# Revit family: LTV8FF
name_source: partatom
category: Lighting Fixtures
units: mm (PartAtom-declared; Revit-internal decimal feet)

## family parameters
Cut with Voids When Loaded = No
Host = Face
Light Source = Yes
OmniClass Number = 23.80.70.14.14
OmniClass Title = Exterior Floodlights
Part Type = Normal
Room Calculation Point = No
Round Connector Dimension = Use Diameter
Shared = No

## types (2) — shared parameters
Color Filter = 16777215
Default Elevation = 48.000"
Description = In cast bronze or stainless steel trim ring, the luminaire is low profile and ADA approved with a drive over weight of 4,500 lbs.
Dimming Lamp Color Temperature Shift = <None>
Emit Shape Visible in Rendering = No
Emit from Circle Diameter = 10.000"
Finish = Bronze
IP Rating = IP68
Lamp = LED
Lens = White Glass
Manufacturer = Kim Lighting
Material = Plastic - Black
Model = Lightvault® 8 Flat Frame
Nominal Watts = 31 W
Tilt Angle = -90.00°
URL = https://www.currentlighting.com
Voltage = 120 V

## per-type parameters (varying)
| type | Apparent Load | Depth | Diameter | Fixture | Photometric Web File | Radius | Wattage Comments |
| LTV81FF | 31 VA | 10.000" | 13.000" | LTV8 : LTV81FF | LTV81FF-SP-24RGBWUV.ies | 6.500" | 31W |
| LTV82FF | 0 VA | 9.875" | 10.375" | LTV8 : LTV82FF | LTV81FF-NF-24RGBWUV.ies | 5.188" |  |

## geometry (parser evidence)
native form markers: Blend x18, Sweep x4
no freeform markers — native parametric forms only
